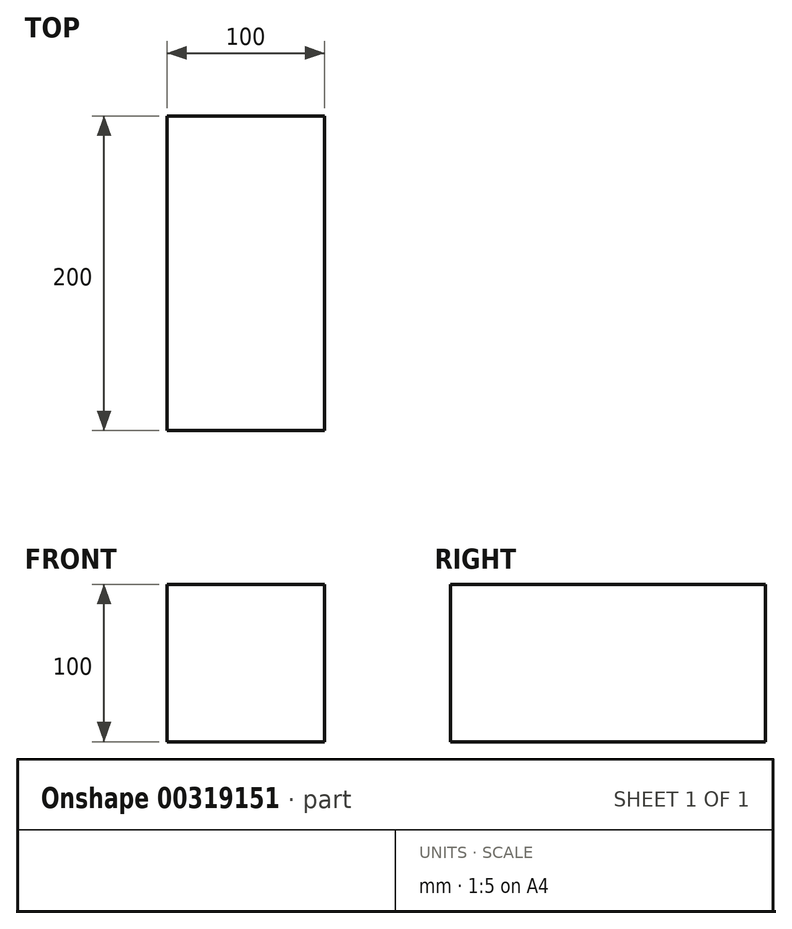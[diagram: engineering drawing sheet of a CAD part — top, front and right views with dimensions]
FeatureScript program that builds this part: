
annotation { "Feature Type Name" : "Feature", "Feature Type Description" : "" }
export const myFeature = defineFeature(function(context is Context, id is Id, definition is map)
    precondition{}
    {
        {
            var Q0;
            Q0=qCreatedBy(makeId("Top.planeOp"),FACE);
            var sketch = newSketch(context, id + "F0", { "sketchPlane" : qUnion([Q0])});
            skLineSegment(sketch, "E0.bottom", {"start": v(-50, 100) * mm, "end": v(50, 100) * mm});
            skLineSegment(sketch, "E0.top", {"start": v(-50, -100) * mm, "end": v(50, -100) * mm});
            skLineSegment(sketch, "E0.left", {"start": v(-50, 100) * mm, "end": v(-50, -100) * mm});
            skLineSegment(sketch, "E0.right", {"start": v(50, 100) * mm, "end": v(50, -100) * mm});
            skPoint(sketch, "E0.middle", {"position": v(0, 0) * mm});
            skSolve(sketch);
        }
        {
            var Q0;
            Q0=makeQuery(id+"F0.imprint","IMPRINT",FACE,{"disambiguationData":[TD([[makeQuery(id+"F0.imprint","IMPRINT",EDGE,{"derivedFrom":sQuery(id+"F0.wireOp",EDGE,"E0.bottom")}),-1.0]])]});
            extrude(context, id + "F1", {"entities" : qUnion([Q0]), "depth" : 100 * mm});
        }
    });
